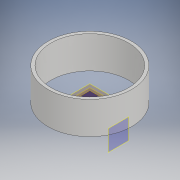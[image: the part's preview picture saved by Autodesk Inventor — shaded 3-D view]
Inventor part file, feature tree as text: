
AUTODESK INVENTOR PART (.ipt)
format: ipt  version: 2019 (Build 230136000, 136)  size: 134,656 bytes
history: native  units: in
note: dims shown in document units (in); Inventor stores cm internally (conversion verified against a paired STEP export)
features: plane x6, sketch x5, extrude x4, projected_geometry x1
ambient origin geometry x8: Origin, YZ Plane, XZ Plane, XY Plane, X Axis, Y Axis, Z Axis, Center Point
bodies: Solid1 (feature_tree)
feature tree (16):
  plane  "Work Plane13"
  sketch  "Sketch6"  dims[d20=0.5315in d47=3.25in]
  plane  "Work Plane14"
  extrude  "Extrusion11"  Depth=3.25in
  plane  "Work Plane10"
  extrude  "Extrusion12"  Depth=0.1in TaperAngle=0.0deg
  plane  "Work Plane9"
  extrude  "Extrusion14"  Depth=1.25in TaperAngle=0.0deg
  extrude  "Extrusion15"  Depth=0.25in TaperAngle=0.0deg
  plane  "Work Plane12"
  plane  "Work Plane11"
  sketch  "Sketch15"  dims[d48=3.5in d49=0.1in d50=0.0in]
  sketch  "Sketch16"  dims[d51=3.25in d52=1.25in d53=0.0in]
  sketch  "Sketch19"  dims[d82=0.25in d83=0.0in d84=0.25in d85=0.0in]
  sketch  "Sketch20"
  projected_geometry  "Projected Loop13"
